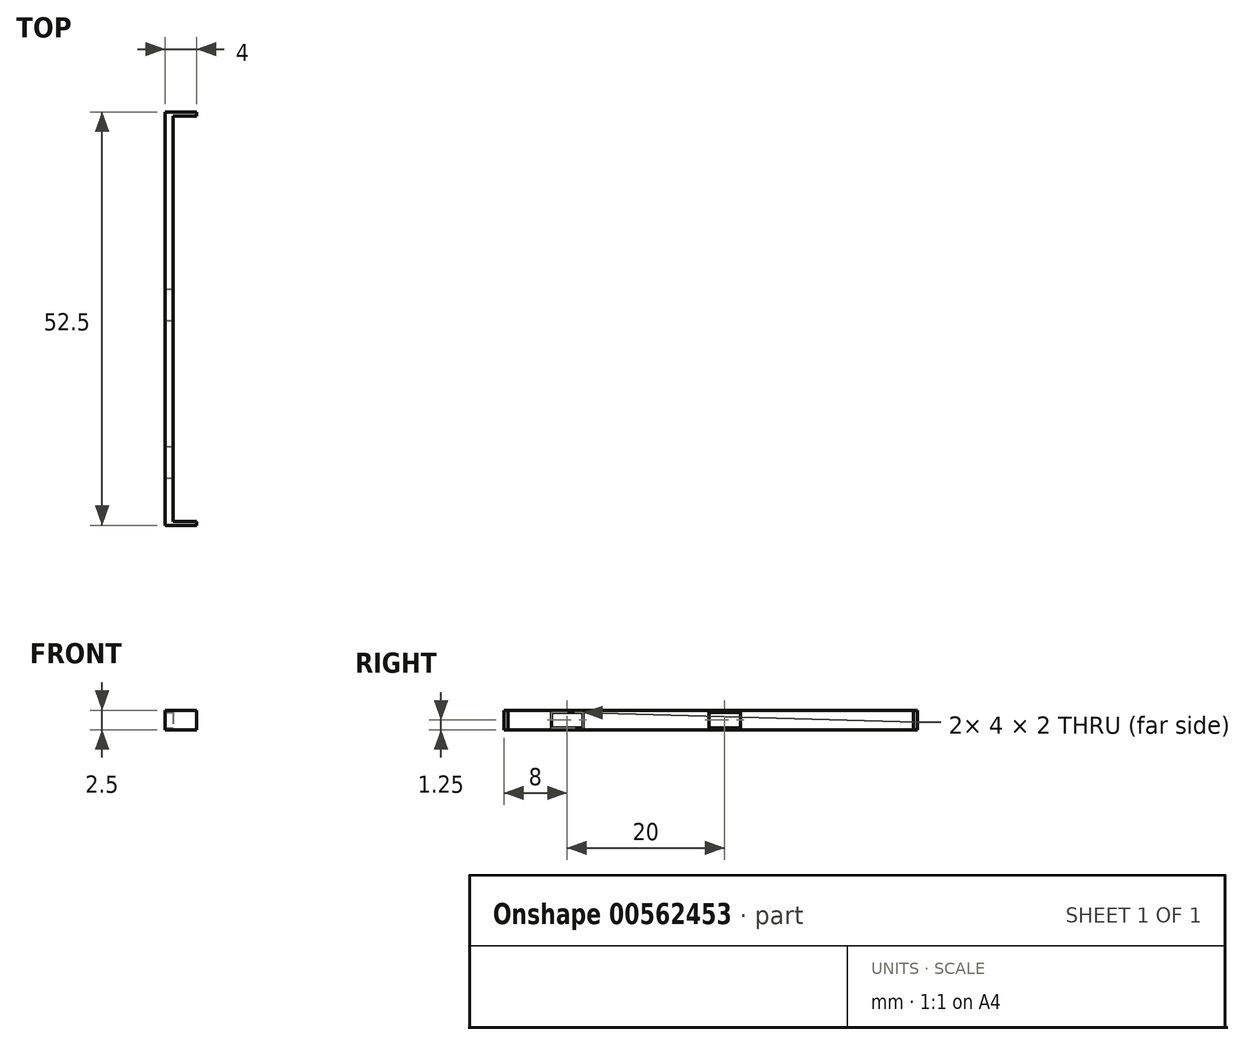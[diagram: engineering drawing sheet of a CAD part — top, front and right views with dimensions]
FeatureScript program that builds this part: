
annotation { "Feature Type Name" : "Feature", "Feature Type Description" : "" }
export const myFeature = defineFeature(function(context is Context, id is Id, definition is map)
    precondition{}
    {
        {
            var Q0;
            Q0=qCreatedBy(makeId("Right.planeOp"),FACE);
            var sketch = newSketch(context, id + "F0", { "sketchPlane" : qUnion([Q0])});
            skLineSegment(sketch, "E0.bottom", {"start": v(-26.25, 1.25) * mm, "end": v(26.25, 1.25) * mm});
            skLineSegment(sketch, "E0.top", {"start": v(-26.25, -1.25) * mm, "end": v(26.25, -1.25) * mm});
            skLineSegment(sketch, "E0.left", {"start": v(-26.25, 1.25) * mm, "end": v(-26.25, -1.25) * mm});
            skLineSegment(sketch, "E0.right", {"start": v(26.25, 1.25) * mm, "end": v(26.25, -1.25) * mm});
            skPoint(sketch, "E0.middle", {"position": v(0, 0) * mm});
            skSolve(sketch);
        }
        {
            var Q0;
            Q0 = qSketchRegion(id + "F0", true);
            extrude(context, id + "F1", {"entities" : qUnion([Q0]), "depth" : 1 * mm, "offsetDistance" : 25 * mm});
        }
        {
            var Q0;
            Q0=makeQuery(id+"F1.opExtrude","CAP_FACE",FACE,{"disambiguationData":[OSD([sQuery(id+"F0.wireOp",EDGE,"E0.bottom"),sQuery(id+"F0.wireOp",EDGE,"E0.top"),sQuery(id+"F0.wireOp",EDGE,"E0.left"),sQuery(id+"F0.wireOp",EDGE,"E0.right")])],"isStart":false});
            var sketch = newSketch(context, id + "F2", { "sketchPlane" : qUnion([Q0])});
            skLineSegment(sketch, "E1.bottom", {"start": v(-26.25, 1.25) * mm, "end": v(-25.75, 1.25) * mm});
            skLineSegment(sketch, "E1.top", {"start": v(-26.25, -1.25) * mm, "end": v(-25.75, -1.25) * mm});
            skLineSegment(sketch, "E1.left", {"start": v(-26.25, 1.25) * mm, "end": v(-26.25, -1.25) * mm});
            skLineSegment(sketch, "E1.right", {"start": v(-25.75, 1.25) * mm, "end": v(-25.75, -1.25) * mm});
            skLineSegment(sketch, "E2.bottom", {"start": v(26.25, 1.25) * mm, "end": v(25.75, 1.25) * mm});
            skLineSegment(sketch, "E2.top", {"start": v(26.25, -1.25) * mm, "end": v(25.75, -1.25) * mm});
            skLineSegment(sketch, "E2.left", {"start": v(26.25, 1.25) * mm, "end": v(26.25, -1.25) * mm});
            skLineSegment(sketch, "E2.right", {"start": v(25.75, 1.25) * mm, "end": v(25.75, -1.25) * mm});
            skSolve(sketch);
        }
        {
            var Q0;
            Q0 = qSketchRegion(id + "F2", true);
            extrude(context, id + "F3", {"entities" : qUnion([Q0]), "operationType" : NewBodyOperationType.ADD, "depth" : 3 * mm, "offsetDistance" : 25 * mm});
        }
        {
            var Q0;
            Q0=makeQuery(id+"F1.opExtrude","CAP_FACE",FACE,{"disambiguationData":[OSD([sQuery(id+"F0.wireOp",EDGE,"E0.bottom"),sQuery(id+"F0.wireOp",EDGE,"E0.top"),sQuery(id+"F0.wireOp",EDGE,"E0.left"),sQuery(id+"F0.wireOp",EDGE,"E0.right")])],"isStart":false});
            var sketch = newSketch(context, id + "F4", { "sketchPlane" : qUnion([Q0])});
            skLineSegment(sketch, "E3.bottom", {"start": v(-20.25, 1) * mm, "end": v(-16.25, 1) * mm});
            skLineSegment(sketch, "E3.top", {"start": v(-20.25, -1) * mm, "end": v(-16.25, -1) * mm});
            skLineSegment(sketch, "E3.left", {"start": v(-20.25, 1) * mm, "end": v(-20.25, -1) * mm});
            skLineSegment(sketch, "E3.right", {"start": v(-16.25, 1) * mm, "end": v(-16.25, -1) * mm});
            skPoint(sketch, "E3.middle", {"position": v(-18.25, 0) * mm});
            skLineSegment(sketch, "E4.bottom", {"start": v(3.75, 1) * mm, "end": v(-0.25, 1) * mm});
            skLineSegment(sketch, "E4.top", {"start": v(3.75, -1) * mm, "end": v(-0.25, -1) * mm});
            skLineSegment(sketch, "E4.left", {"start": v(3.75, 1) * mm, "end": v(3.75, -1) * mm});
            skLineSegment(sketch, "E4.right", {"start": v(-0.25, 1) * mm, "end": v(-0.25, -1) * mm});
            skPoint(sketch, "E4.middle", {"position": v(1.75, 0) * mm});
            skSolve(sketch);
        }
        {
            var Q0;
            Q0 = qSketchRegion(id + "F4", true);
            extrude(context, id + "F5", {"entities" : qUnion([Q0]), "operationType" : NewBodyOperationType.REMOVE, "endBound" : BoundingType.UP_TO_NEXT, "oppositeDirection" : true, "depth" : 25 * mm, "offsetDistance" : 25 * mm});
        }
    });
